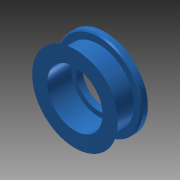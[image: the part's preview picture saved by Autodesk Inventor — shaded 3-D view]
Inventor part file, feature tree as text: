
AUTODESK INVENTOR PART (.ipt)
format: ipt  version: 2013 (Build 170138000, 138)  size: 117,760 bytes
history: native  units: mm
features: revolve x1, sketch x1
ambient origin geometry x8: Origin, YZ Plane, XZ Plane, XY Plane, X Axis, Y Axis, Z Axis, Center Point
bodies: Solid1 (feature_tree)
feature tree (2):
  revolve  "Revolution1"  [1 undecoded]
  sketch  "Sketch1"  dims[d6=12.0mm d7=11.0mm d10=90.0deg d14=6.0mm d17=7.0mm d18=2.5mm d19=135.0deg d20=3.0mm d21=2.0mm d22=2.5mm]
note: 1 required parameter value undecoded (feature->parameter linkage not recoverable at this tier; creation-order binding heuristic only, values carry confidence <= 0.55)
